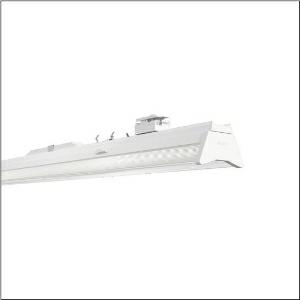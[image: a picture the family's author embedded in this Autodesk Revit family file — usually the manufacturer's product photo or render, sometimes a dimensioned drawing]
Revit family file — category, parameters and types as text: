
# Revit family: licross_r__21_performance_mo_52td167n485g_efc6
name_source: partatom
category: Lighting Fixtures
units: mm (PartAtom-declared; Revit-internal decimal feet)

## family parameters
Cut with Voids When Loaded = No
Host = Face
Light Source = No
Part Type = Normal
Room Calculation Point = No
Round Connector Dimension = Use Diameter
Shared = No

## types (1)
- Licross® 21 Performance MO (1 x LED, 8720 lm, 47.9 W, 4000K)
    Apparent Load = 48 VA
    CIE Flux Codes = 66 88 96 79 100
    Color Rendering = 80
    Color Temperature = 4000K
    Default Elevation = 1800 mm
    Description = Licross® 21 Performance MO, luminaire insert, of sheet steel, galvanised, coil coated, white, length: 1.500mm, width: 120mm, height: 123mm, LED rated luminous flux: 8.720lm, light colour: 840, control gear: ON/OFF, with plug, 3-pole, with phase selection, mains connection: 220..240V, AC, 50/60Hz, rated input power: 48W, halogen-free wiring, primary light control with lens, of plastic, primary optical cover: cover, of PMMA, light emission: direct/indirect distribution, primary light characteristic: symmetric, protection rating (complete): IP54, insulation class (complete): insulation class I (protective earthing), certification: CE, ENEC, UKCA, protection symbol: D if used in an environment with non-conductive dust loads with corresponding accessories, impact resistance: IK06, permissible ambient temperature for indoor applications: -35..+45°C, corresponds to IFS (International Featured Standards) requirements for safety and quality in the food industry, reducing of maximum allowable ambient temperature of 5°C with ceiling mounting, LABS conformity tested according to VDMA 24364:2018-05, packaging unit: 1 piece
    Height = 114 mm
    Lamp = 1 x LED
    Lamp Light Flux = 8720 lm
    Lamp Power = 47.9 W
    Lamp count = 1
    Length = 1500 mm
    Luminous efficacy = 182 lm/W
    Manufacturer = Siteco
    ModVariant = No
    Model = 52TD167N485G
    Mounting Place = Ceiling
    Mounting Type = Pendant
    Number of Poles = 1
    OnlyDefault = Yes
    Power Factor = 1
    Product Name = Licross® 21 Performance MO
    Product group = luminaire insert
    ProductGroupID = 902
    Protection Class = Protection class I
    Protection Degree = IP 54
    RLX_Detail_Level = 1
    RLX_Emergency_Light_Flux = 0 lm
    RLX_Emergency_Type = 0
    RLX_Emergency_Type_DB = No
    RlxData = <blob elided: 30389 chars, md5=c264e259>
    Socket = socket
    Standby Power = 0 W
    System Light Flux = 8720 lm
    System Power = 48 W
    Type Comments = Product without accessories
    Type Image = l_1256138.jpg
    URL = http://relux.com
    VarID = ---
    Voltage = 0 V
    Weight = 0.00 kg
    Width = 120 mm

## geometry (parser evidence)
native form markers: Blend x4, Sweep x14
no freeform markers — native parametric forms only
